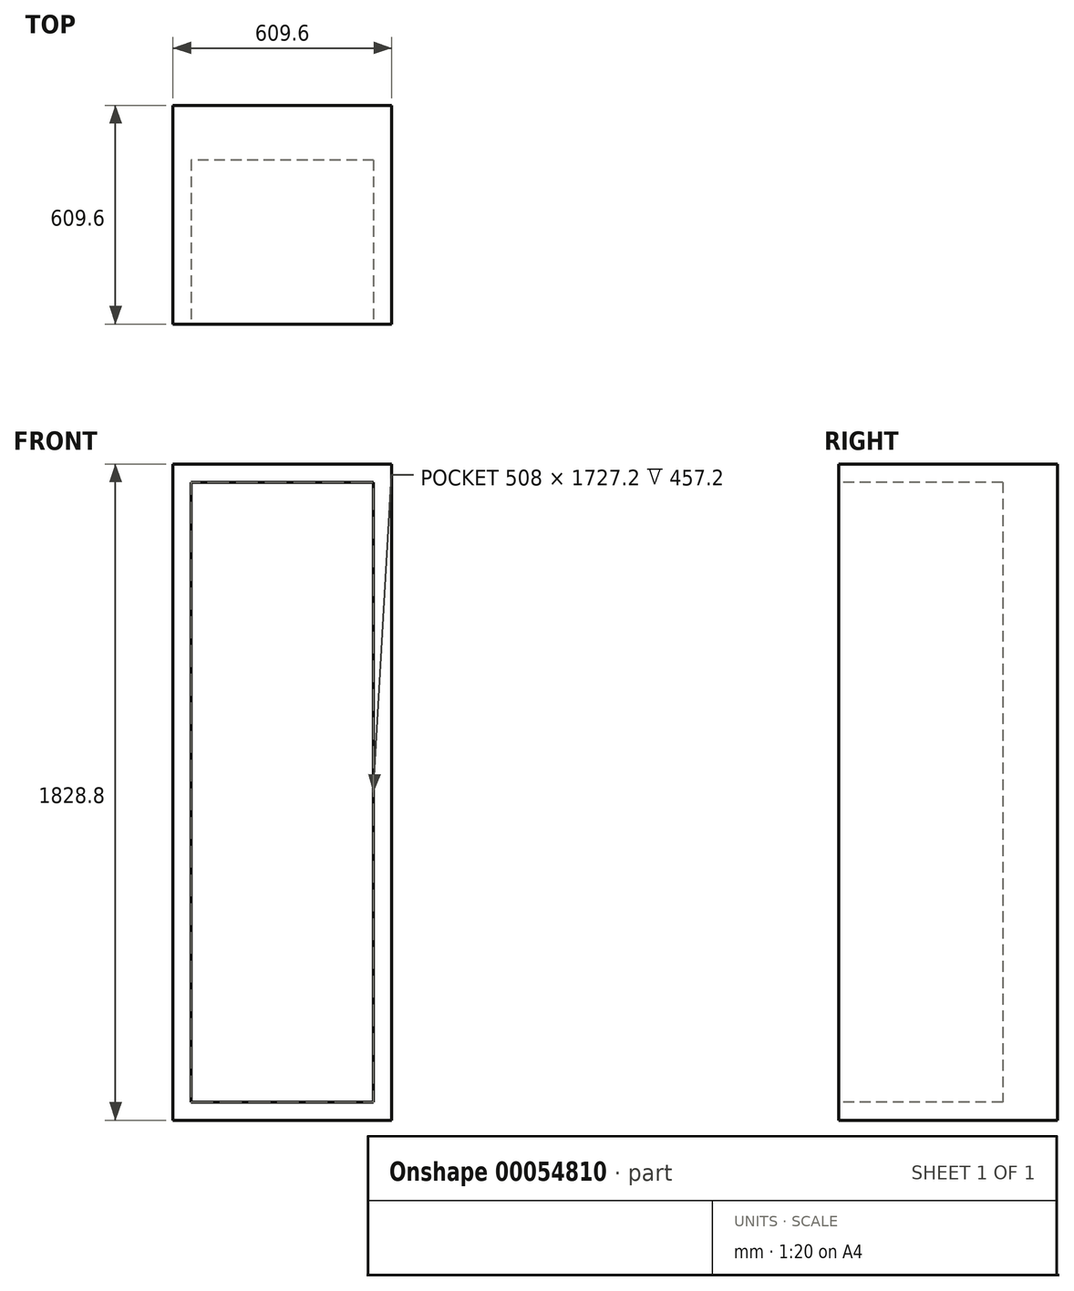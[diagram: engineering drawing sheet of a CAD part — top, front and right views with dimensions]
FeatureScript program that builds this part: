
annotation { "Feature Type Name" : "Feature", "Feature Type Description" : "" }
export const myFeature = defineFeature(function(context is Context, id is Id, definition is map)
    precondition{}
    {
        {
            var Q0;
            Q0=qCreatedBy(makeId("Top.planeOp"),FACE);
            var sketch = newSketch(context, id + "F0", { "sketchPlane" : qUnion([Q0])});
            skLineSegment(sketch, "E0.bottom", {"start": v(361.09, 322.1) * mm, "end": v(-248.51, 322.1) * mm});
            skLineSegment(sketch, "E0.top", {"start": v(361.09, -287.5) * mm, "end": v(-248.51, -287.5) * mm});
            skLineSegment(sketch, "E0.left", {"start": v(361.09, 322.1) * mm, "end": v(361.09, -287.5) * mm});
            skLineSegment(sketch, "E0.right", {"start": v(-248.51, 322.1) * mm, "end": v(-248.51, -287.5) * mm});
            skSolve(sketch);
        }
        {
            var Q0;
            Q0=makeQuery(id+"F0.imprint","IMPRINT",FACE,{"disambiguationData":[TD([[makeQuery(id+"F0.imprint","IMPRINT",EDGE,{"derivedFrom":sQuery(id+"F0.wireOp",EDGE,"E0.bottom")}),1.0]])]});
            extrude(context, id + "F3", {"entities" : qUnion([Q0]), "depth" : 1828.8 * mm});
        }
        {
            var Q0;
            Q0=makeQuery(id+"F3.opExtrude","SWEPT_FACE",FACE,{"disambiguationData":[OSD([sQuery(id+"F0.wireOp",EDGE,"E0.top")])]});
            var sketch = newSketch(context, id + "F1", { "sketchPlane" : qUnion([Q0])});
            skLineSegment(sketch, "E1.0", {"start": v(-299.31, 1879.6) * mm, "end": v(-299.31, -50.8) * mm});
            skLineSegment(sketch, "E1.1", {"start": v(411.89, 1879.6) * mm, "end": v(-299.31, 1879.6) * mm});
            skLineSegment(sketch, "E1.2", {"start": v(411.89, 1879.6) * mm, "end": v(411.89, -50.8) * mm});
            skLineSegment(sketch, "E1.3", {"start": v(411.89, -50.8) * mm, "end": v(-299.31, -50.8) * mm});
            skLineSegment(sketch, "E2.0", {"start": v(310.29, 1778) * mm, "end": v(310.29, 50.8) * mm});
            skLineSegment(sketch, "E2.1", {"start": v(310.29, 1778) * mm, "end": v(-197.71, 1778) * mm});
            skLineSegment(sketch, "E2.2", {"start": v(-197.71, 1778) * mm, "end": v(-197.71, 50.8) * mm});
            skLineSegment(sketch, "E2.3", {"start": v(310.29, 50.8) * mm, "end": v(-197.71, 50.8) * mm});
            skSolve(sketch);
        }
        {
            var Q0;
            Q0=makeQuery(id+"F1.imprint","IMPRINT",FACE,{"disambiguationData":[TD([[makeQuery(id+"F1.imprint","IMPRINT",EDGE,{"derivedFrom":sQuery(id+"F1.wireOp",EDGE,"E2.0")}),-1.0]])]});
            extrude(context, id + "F4", {"entities" : qUnion([Q0]), "operationType" : NewBodyOperationType.REMOVE, "oppositeDirection" : true, "depth" : 457.2 * mm});
        }
    });
